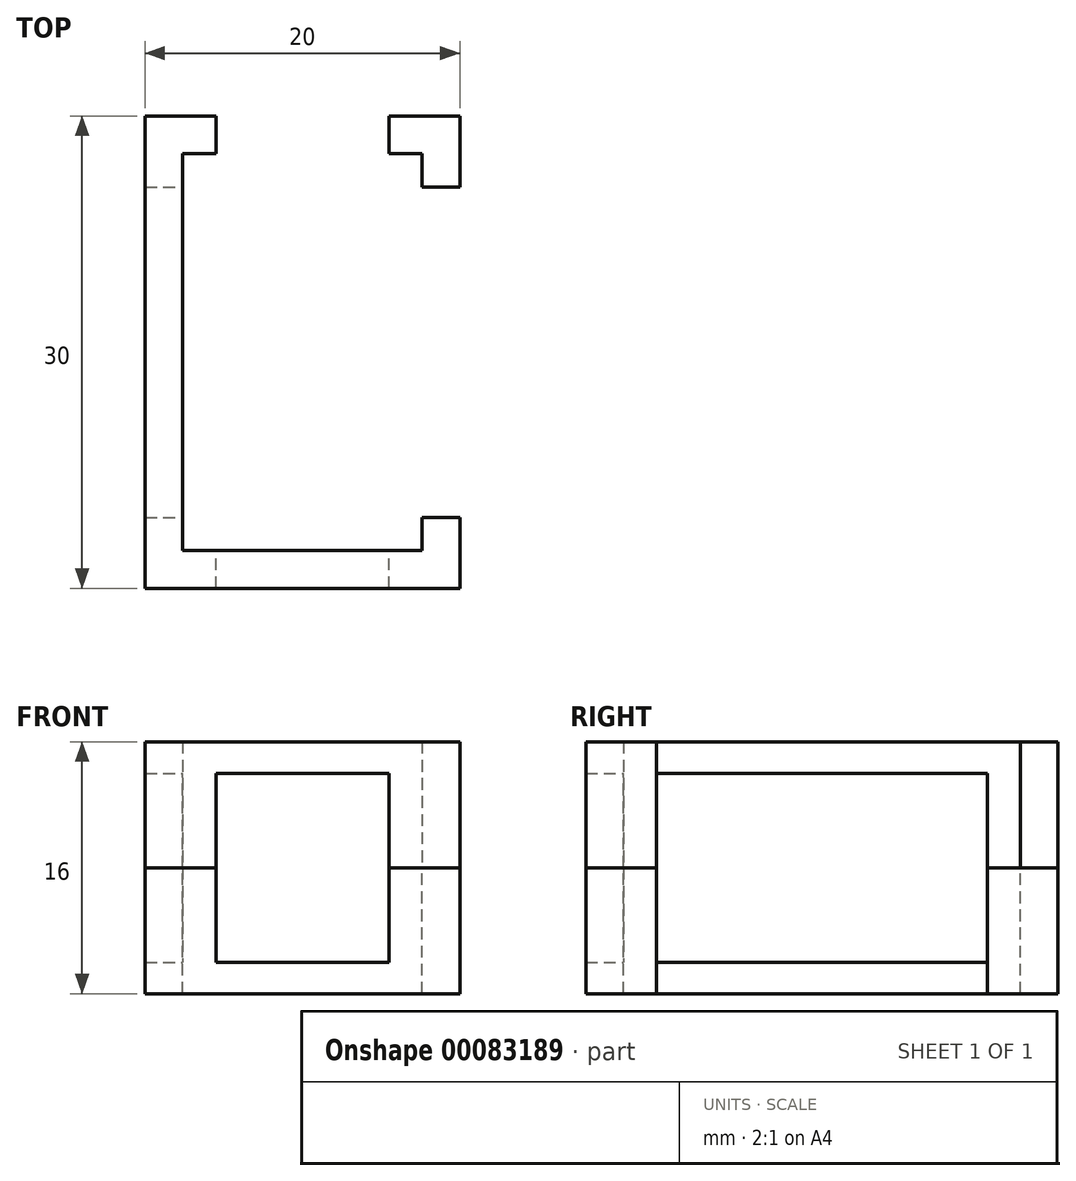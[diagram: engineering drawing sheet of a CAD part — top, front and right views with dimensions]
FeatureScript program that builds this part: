
annotation { "Feature Type Name" : "Feature", "Feature Type Description" : "" }
export const myFeature = defineFeature(function(context is Context, id is Id, definition is map)
    precondition{}
    {
        {
            var Q0;
            Q0=qCreatedBy(makeId("Top.planeOp"),FACE);
            var sketch = newSketch(context, id + "F0", { "sketchPlane" : qUnion([Q0])});
            skLineSegment(sketch, "E0.bottom", {"start": v(-38.64, -31.51) * mm, "end": v(-53.84, -31.51) * mm});
            skLineSegment(sketch, "E0.top", {"start": v(-38.64, -6.31) * mm, "end": v(-53.84, -6.31) * mm});
            skLineSegment(sketch, "E0.left", {"start": v(-38.64, -31.51) * mm, "end": v(-38.64, -6.31) * mm});
            skLineSegment(sketch, "E0.right", {"start": v(-53.84, -31.51) * mm, "end": v(-53.84, -6.31) * mm});
            skPoint(sketch, "E1", {"position": v(-49.44, -6.31) * mm});
            skPoint(sketch, "E2", {"position": v(-38.64, -27.41) * mm});
            skLineSegment(sketch, "E3.1.0.0", {"start": v(-38.64, -26.16) * mm, "end": v(-38.64, -25.16) * mm});
            skPoint(sketch, "E3.1.0.1", {"position": v(-38.64, -26.16) * mm});
            skLineSegment(sketch, "E3.2.0.0", {"start": v(-38.64, -24.91) * mm, "end": v(-38.64, -23.91) * mm});
            skPoint(sketch, "E3.2.0.1", {"position": v(-38.64, -24.91) * mm});
            skLineSegment(sketch, "E3.3.0.0", {"start": v(-38.64, -23.66) * mm, "end": v(-38.64, -22.66) * mm});
            skPoint(sketch, "E3.3.0.1", {"position": v(-38.64, -23.66) * mm});
            skLineSegment(sketch, "E4.0.8.0", {"start": v(-38.64, -17.41) * mm, "end": v(-38.64, -16.41) * mm});
            skPoint(sketch, "E4.3.8.0", {"position": v(-38.64, -17.41) * mm});
            skLineSegment(sketch, "E4.0.9.0", {"start": v(-38.64, -16.16) * mm, "end": v(-38.64, -15.16) * mm});
            skPoint(sketch, "E4.3.9.0", {"position": v(-38.64, -16.16) * mm});
            skLineSegment(sketch, "E5.bottom", {"start": v(-49.44, -6.31) * mm, "end": v(-48.44, -6.31) * mm});
            skPoint(sketch, "E6.1.0.1", {"position": v(-48.19, -6.31) * mm});
            skLineSegment(sketch, "E6.1.0.4", {"start": v(-48.19, -6.31) * mm, "end": v(-47.19, -6.31) * mm});
            skPoint(sketch, "E6.2.0.1", {"position": v(-46.94, -6.31) * mm});
            skLineSegment(sketch, "E6.2.0.4", {"start": v(-46.94, -6.31) * mm, "end": v(-45.94, -6.31) * mm});
            skPoint(sketch, "E6.3.0.1", {"position": v(-45.69, -6.31) * mm});
            skLineSegment(sketch, "E6.3.0.4", {"start": v(-45.69, -6.31) * mm, "end": v(-44.69, -6.31) * mm});
            skPoint(sketch, "E6.4.0.1", {"position": v(-44.44, -6.31) * mm});
            skLineSegment(sketch, "E6.4.0.4", {"start": v(-44.44, -6.31) * mm, "end": v(-43.44, -6.31) * mm});
            skLineSegment(sketch, "E7.bottom", {"start": v(-36.24, -33.91) * mm, "end": v(-56.24, -33.91) * mm});
            skLineSegment(sketch, "E7.top", {"start": v(-36.24, -3.91) * mm, "end": v(-56.24, -3.91) * mm});
            skLineSegment(sketch, "E7.left", {"start": v(-36.24, -33.91) * mm, "end": v(-36.24, -3.91) * mm});
            skLineSegment(sketch, "E7.right", {"start": v(-56.24, -33.91) * mm, "end": v(-56.24, -3.91) * mm});
            skLineSegment(sketch, "E8.bottom", {"start": v(-42.24, -16.16) * mm, "end": v(-50.24, -16.16) * mm});
            skLineSegment(sketch, "E8.top", {"start": v(-42.24, -8.66) * mm, "end": v(-50.24, -8.66) * mm});
            skLineSegment(sketch, "E8.left", {"start": v(-42.24, -16.16) * mm, "end": v(-42.24, -8.66) * mm});
            skLineSegment(sketch, "E8.right", {"start": v(-50.24, -16.16) * mm, "end": v(-50.24, -8.66) * mm});
            skPoint(sketch, "E9", {"position": v(-39.24, -24.41) * mm});
            skPoint(sketch, "E9.positionSnap0", {"position": v(-39.84, -24.41) * mm});
            skPoint(sketch, "E9.positionSnap1", {"position": v(-39.24, -24.91) * mm});
            skPoint(sketch, "E10", {"position": v(-39.24, -23.16) * mm});
            skPoint(sketch, "E10.positionSnap0", {"position": v(-39.84, -23.16) * mm});
            skPoint(sketch, "E10.positionSnap1", {"position": v(-39.24, -23.66) * mm});
            skPoint(sketch, "E11", {"position": v(-39.24, -16.91) * mm});
            skPoint(sketch, "E11.positionSnap0", {"position": v(-39.84, -16.91) * mm});
            skPoint(sketch, "E11.positionSnap1", {"position": v(-39.24, -17.41) * mm});
            skPoint(sketch, "E12", {"position": v(-39.24, -15.66) * mm});
            skPoint(sketch, "E12.positionSnap0", {"position": v(-39.84, -15.66) * mm});
            skPoint(sketch, "E12.positionSnap1", {"position": v(-39.24, -16.16) * mm});
            skPoint(sketch, "E13", {"position": v(-43.94, -6.91) * mm});
            skPoint(sketch, "E13.positionSnap0", {"position": v(-43.94, -7.51) * mm});
            skPoint(sketch, "E13.positionSnap1", {"position": v(-43.44, -6.91) * mm});
            skPoint(sketch, "E14", {"position": v(-45.19, -6.91) * mm});
            skPoint(sketch, "E14.positionSnap0", {"position": v(-45.19, -7.51) * mm});
            skPoint(sketch, "E14.positionSnap1", {"position": v(-45.69, -6.91) * mm});
            skPoint(sketch, "E15", {"position": v(-46.44, -6.91) * mm});
            skPoint(sketch, "E15.positionSnap0", {"position": v(-46.44, -7.51) * mm});
            skPoint(sketch, "E15.positionSnap1", {"position": v(-46.94, -6.91) * mm});
            skPoint(sketch, "E16", {"position": v(-47.69, -6.91) * mm});
            skPoint(sketch, "E16.positionSnap0", {"position": v(-47.69, -7.51) * mm});
            skPoint(sketch, "E16.positionSnap1", {"position": v(-47.19, -6.91) * mm});
            skPoint(sketch, "E17", {"position": v(-48.94, -6.91) * mm});
            skPoint(sketch, "E17.positionSnap0", {"position": v(-48.94, -6.31) * mm});
            skPoint(sketch, "E17.positionSnap1", {"position": v(-48.44, -6.91) * mm});
            skLineSegment(sketch, "E18", {"start": v(-56.24, -29.41) * mm, "end": v(-53.84, -29.41) * mm});
            skLineSegment(sketch, "E19", {"start": v(-51.74, -33.91) * mm, "end": v(-51.74, -31.51) * mm});
            skLineSegment(sketch, "E20.trimOffspring", {"start": v(-38.64, -29.41) * mm, "end": v(-36.24, -29.41) * mm});
            skLineSegment(sketch, "E21.trimOffspring", {"start": v(-51.74, -6.31) * mm, "end": v(-51.74, -3.91) * mm});
            skLineSegment(sketch, "E22.MirrorCS", {"start": v(-56.24, -8.41) * mm, "end": v(-53.84, -8.41) * mm});
            skLineSegment(sketch, "E23.MirrorCS", {"start": v(-38.64, -8.41) * mm, "end": v(-36.24, -8.41) * mm});
            skLineSegment(sketch, "E24.MirrorCS", {"start": v(-40.74, -33.91) * mm, "end": v(-40.74, -31.51) * mm});
            skLineSegment(sketch, "E25.MirrorCS", {"start": v(-40.74, -6.31) * mm, "end": v(-40.74, -3.91) * mm});
            skLineSegment(sketch, "E26", {"start": v(-53.84, -19.28) * mm, "end": v(-38.64, -19.28) * mm, "construction": true});
            skLineSegment(sketch, "E27", {"start": v(-53.84, -22.02) * mm, "end": v(-38.64, -22.02) * mm, "construction": true});
            skLineSegment(sketch, "E28", {"start": v(-53.84, -25.38) * mm, "end": v(-38.64, -25.38) * mm, "construction": true});
            skLineSegment(sketch, "E29", {"start": v(-53.84, -28.17) * mm, "end": v(-38.64, -28.17) * mm, "construction": true});
            skPoint(sketch, "E30", {"position": v(-49.84, -19.28) * mm});
            skPoint(sketch, "E31", {"position": v(-48.59, -19.28) * mm});
            skPoint(sketch, "E32", {"position": v(-43.89, -19.28) * mm});
            skPoint(sketch, "E33", {"position": v(-49.84, -22.02) * mm});
            skPoint(sketch, "E34", {"position": v(-48.59, -22.02) * mm});
            skPoint(sketch, "E35", {"position": v(-42.64, -22.02) * mm});
            skPoint(sketch, "E36", {"position": v(-43.89, -22.02) * mm});
            skPoint(sketch, "E37", {"position": v(-49.84, -25.38) * mm});
            skPoint(sketch, "E38", {"position": v(-48.59, -25.38) * mm});
            skPoint(sketch, "E39", {"position": v(-43.89, -25.38) * mm});
            skPoint(sketch, "E40", {"position": v(-42.64, -25.38) * mm});
            skPoint(sketch, "E41", {"position": v(-42.64, -19.28) * mm});
            skPoint(sketch, "E42", {"position": v(-39.24, -26.91) * mm});
            skPoint(sketch, "E43", {"position": v(-39.24, -25.66) * mm});
            skSolve(sketch);
        }
        {
            var Q0;
            Q0=makeQuery(id+"F0.imprint","IMPRINT",FACE,{"disambiguationData":[TD([[makeQuery(id+"F0.imprint","IMPRINT",EDGE,{"derivedFrom":sQuery(id+"F0.wireOp",EDGE,"5d814dad-614f-4d97-b61d-e02d43bfdc46")}),-1.0]])]});
            var Q1;
            {var subQ0=sQuery(id+"F0.wireOp",EDGE,"E18");Q1=makeQuery(id+"F0.imprint","IMPRINT",FACE,{"disambiguationData":[TD([[makeQuery(id+"F0.imprint","IMPRINT",EDGE,{"derivedFrom":subQ0}),1.0]])]});}
            var Q2;
            {var subQ0=sQuery(id+"F0.wireOp",EDGE,"E19");Q2=makeQuery(id+"F0.imprint","IMPRINT",FACE,{"disambiguationData":[TD([[makeQuery(id+"F0.imprint","IMPRINT",EDGE,{"derivedFrom":subQ0}),-1.0]])]});}
            var Q3;
            {var subQ3=sQuery(id+"F0.wireOp",EDGE,"E18");Q3=makeQuery(id+"F0.imprint","IMPRINT",FACE,{"disambiguationData":[TD([[makeQuery(id+"F0.imprint","IMPRINT",EDGE,{"derivedFrom":subQ3}),-1.0]])]});}
            var Q4;
            {var subQ4=sQuery(id+"F0.wireOp",EDGE,"E20.trimOffspring");Q4=makeQuery(id+"F0.imprint","IMPRINT",FACE,{"disambiguationData":[TD([[makeQuery(id+"F0.imprint","IMPRINT",EDGE,{"derivedFrom":subQ4}),-1.0]])]});}
            var Q5;
            {var subQ4=sQuery(id+"F0.wireOp",EDGE,"E3.1.0.0");Q5=makeQuery(id+"F0.imprint","IMPRINT",FACE,{"disambiguationData":[TD([[makeQuery(id+"F0.imprint","IMPRINT",EDGE,{"derivedFrom":subQ4}),-1.0]])]});}
            var Q6;
            {var subQ3=sQuery(id+"F0.wireOp",EDGE,"E23.MirrorCS");Q6=makeQuery(id+"F0.imprint","IMPRINT",FACE,{"disambiguationData":[TD([[makeQuery(id+"F0.imprint","IMPRINT",EDGE,{"derivedFrom":subQ3}),1.0]])]});}
            var Q7;
            {var subQ0=sQuery(id+"F0.wireOp",EDGE,"E5.bottom");Q7=makeQuery(id+"F0.imprint","IMPRINT",FACE,{"disambiguationData":[TD([[makeQuery(id+"F0.imprint","IMPRINT",EDGE,{"derivedFrom":subQ0}),1.0]])]});}
            var Q8;
            {var subQ7=sQuery(id+"F0.wireOp",EDGE,"E21.trimOffspring");Q8=makeQuery(id+"F0.imprint","IMPRINT",FACE,{"disambiguationData":[TD([[makeQuery(id+"F0.imprint","IMPRINT",EDGE,{"derivedFrom":subQ7}),1.0]])]});}
            var Q9;
            {var subQ4=sQuery(id+"F0.wireOp",EDGE,"E3.1.0.0");Q9=makeQuery(id+"F0.imprint","IMPRINT",FACE,{"disambiguationData":[TD([[makeQuery(id+"F0.imprint","IMPRINT",EDGE,{"derivedFrom":subQ4}),1.0]])]});}
            extrude(context, id + "F1", {"entities" : qUnion([Q0, Q1, Q2, Q3, Q4, Q5, Q6, Q7, Q8, Q9]), "oppositeDirection" : true, "depth" : 2 * mm});
        }
        {
            var Q0;
            {var subQ4=sQuery(id+"F0.wireOp",EDGE,"E21.trimOffspring");Q0=makeQuery(id+"F0.imprint","IMPRINT",FACE,{"disambiguationData":[TD([[makeQuery(id+"F0.imprint","IMPRINT",EDGE,{"derivedFrom":subQ4}),1.0]])]});}
            var Q1;
            {var subQ3=sQuery(id+"F0.wireOp",EDGE,"E23.MirrorCS");Q1=makeQuery(id+"F0.imprint","IMPRINT",FACE,{"disambiguationData":[TD([[makeQuery(id+"F0.imprint","IMPRINT",EDGE,{"derivedFrom":subQ3}),1.0]])]});}
            var Q2;
            {var subQ3=sQuery(id+"F0.wireOp",EDGE,"E20.trimOffspring");Q2=makeQuery(id+"F0.imprint","IMPRINT",FACE,{"disambiguationData":[TD([[makeQuery(id+"F0.imprint","IMPRINT",EDGE,{"derivedFrom":subQ3}),-1.0]])]});}
            var Q3;
            {var subQ3=sQuery(id+"F0.wireOp",EDGE,"E18");Q3=makeQuery(id+"F0.imprint","IMPRINT",FACE,{"disambiguationData":[TD([[makeQuery(id+"F0.imprint","IMPRINT",EDGE,{"derivedFrom":subQ3}),-1.0]])]});}
            extrude(context, id + "F2", {"entities" : qUnion([Q0, Q1, Q2, Q3]), "operationType" : NewBodyOperationType.ADD, "depth" : 6 * mm});
        }
        {
            var Q0;
            Q0=sQuery(id+"F0.wireOp",VERTEX,"E9");
            var Q1;
            Q1=sQuery(id+"F0.wireOp",VERTEX,"E10");
            var Q2;
            Q2=sQuery(id+"F0.wireOp",VERTEX,"E11");
            var Q3;
            Q3=sQuery(id+"F0.wireOp",VERTEX,"E12");
            var Q4;
            Q4=sQuery(id+"F0.wireOp",VERTEX,"E13");
            var Q5;
            Q5=sQuery(id+"F0.wireOp",VERTEX,"E14");
            var Q6;
            Q6=sQuery(id+"F0.wireOp",VERTEX,"E15");
            var Q7;
            Q7=sQuery(id+"F0.wireOp",VERTEX,"E16");
            var Q8;
            Q8=sQuery(id+"F0.wireOp",VERTEX,"E17");
            var Q9;
            Q9=sQuery(id+"F0.wireOp",VERTEX,"E43");
            var Q10;
            Q10=sQuery(id+"F0.wireOp",VERTEX,"E42");
            var Q11;
            Q11=makeQuery(id+"F1.opExtrude","SWEPT_BODY",BODY,{"disambiguationData":[OSD([sQuery(id+"F0.wireOp",EDGE,"E7.bottom"),sQuery(id+"F0.wireOp",EDGE,"E7.top"),sQuery(id+"F0.wireOp",EDGE,"E7.left"),sQuery(id+"F0.wireOp",EDGE,"E7.right"),sQuery(id+"F0.wireOp",EDGE,"E8.bottom"),sQuery(id+"F0.wireOp",EDGE,"E8.top"),sQuery(id+"F0.wireOp",EDGE,"E8.left"),sQuery(id+"F0.wireOp",EDGE,"E8.right")])]});
            hole(context, id + "F3", {"style" : HoleStyle.SIMPLE, "endStyle" : HoleEndStyle.THROUGH, "holeDiameter" : 1.1 * mm, "locations" : qUnion([Q0, Q1, Q2, Q3, Q4, Q5, Q6, Q7, Q8, Q9, Q10]), "scope" : qUnion([Q11]), "isTappedThrough" : true});
        }
        {
            var Q0;
            Q0=sQuery(id+"F0.wireOp",VERTEX,"E30");
            var Q1;
            Q1=sQuery(id+"F0.wireOp",VERTEX,"E31");
            var Q2;
            Q2=sQuery(id+"F0.wireOp",VERTEX,"E32");
            var Q3;
            Q3=sQuery(id+"F0.wireOp",VERTEX,"E41");
            var Q4;
            Q4=sQuery(id+"F0.wireOp",VERTEX,"E33");
            var Q5;
            Q5=sQuery(id+"F0.wireOp",VERTEX,"E34");
            var Q6;
            Q6=sQuery(id+"F0.wireOp",VERTEX,"E36");
            var Q7;
            Q7=sQuery(id+"F0.wireOp",VERTEX,"E35");
            var Q8;
            Q8=makeQuery(id+"F1.opExtrude","SWEPT_BODY",BODY,{"disambiguationData":[OSD([sQuery(id+"F0.wireOp",EDGE,"E7.bottom"),sQuery(id+"F0.wireOp",EDGE,"E7.top"),sQuery(id+"F0.wireOp",EDGE,"E7.left"),sQuery(id+"F0.wireOp",EDGE,"E7.right"),sQuery(id+"F0.wireOp",EDGE,"E8.bottom"),sQuery(id+"F0.wireOp",EDGE,"E8.top"),sQuery(id+"F0.wireOp",EDGE,"E8.left"),sQuery(id+"F0.wireOp",EDGE,"E8.right")])]});
            hole(context, id + "F4", {"style" : HoleStyle.SIMPLE, "endStyle" : HoleEndStyle.THROUGH, "holeDiameter" : 1.1 * mm, "locations" : qUnion([Q0, Q1, Q2, Q3, Q4, Q5, Q6, Q7]), "scope" : qUnion([Q8]), "isTappedThrough" : true});
        }
        {
            var Q0;
            Q0=sQuery(id+"F0.wireOp",VERTEX,"E37");
            var Q1;
            Q1=sQuery(id+"F0.wireOp",VERTEX,"E38");
            var Q2;
            Q2=sQuery(id+"F0.wireOp",VERTEX,"E39");
            var Q3;
            Q3=sQuery(id+"F0.wireOp",VERTEX,"E40");
            var Q4;
            Q4=makeQuery(id+"F1.opExtrude","SWEPT_BODY",BODY,{"disambiguationData":[OSD([sQuery(id+"F0.wireOp",EDGE,"E7.bottom"),sQuery(id+"F0.wireOp",EDGE,"E7.top"),sQuery(id+"F0.wireOp",EDGE,"E7.left"),sQuery(id+"F0.wireOp",EDGE,"E7.right"),sQuery(id+"F0.wireOp",EDGE,"E8.bottom"),sQuery(id+"F0.wireOp",EDGE,"E8.top"),sQuery(id+"F0.wireOp",EDGE,"E8.left"),sQuery(id+"F0.wireOp",EDGE,"E8.right")])]});
            hole(context, id + "F5", {"style" : HoleStyle.SIMPLE, "endStyle" : HoleEndStyle.THROUGH, "holeDiameter" : 1 * mm, "locations" : qUnion([Q0, Q1, Q2, Q3]), "scope" : qUnion([Q4]), "isTappedThrough" : true});
        }
        {
            var Q0;
            Q0=makeQuery(id+"F1.opExtrude","SWEPT_BODY",BODY,{"disambiguationData":[OSD([sQuery(id+"F0.wireOp",EDGE,"E7.bottom"),sQuery(id+"F0.wireOp",EDGE,"E7.top"),sQuery(id+"F0.wireOp",EDGE,"E7.left"),sQuery(id+"F0.wireOp",EDGE,"E7.right"),sQuery(id+"F0.wireOp",EDGE,"E8.bottom"),sQuery(id+"F0.wireOp",EDGE,"E8.top"),sQuery(id+"F0.wireOp",EDGE,"E8.left"),sQuery(id+"F0.wireOp",EDGE,"E8.right")])]});
            var Q1;
            Q1=makeQuery(id+"F2.opExtrude","CAP_FACE",FACE,{"disambiguationData":[OSD([sQuery(id+"F0.wireOp",EDGE,"E0.top"),sQuery(id+"F0.wireOp",EDGE,"E0.right"),sQuery(id+"F0.wireOp",EDGE,"E7.top"),sQuery(id+"F0.wireOp",EDGE,"E7.right"),sQuery(id+"F0.wireOp",EDGE,"E21.trimOffspring"),sQuery(id+"F0.wireOp",EDGE,"E22.MirrorCS")])],"isStart":false});
            mirror(context, id + "F6", {"entities" : qUnion([Q0]), "mirrorPlane" : qUnion([Q1])});
        }
    });
